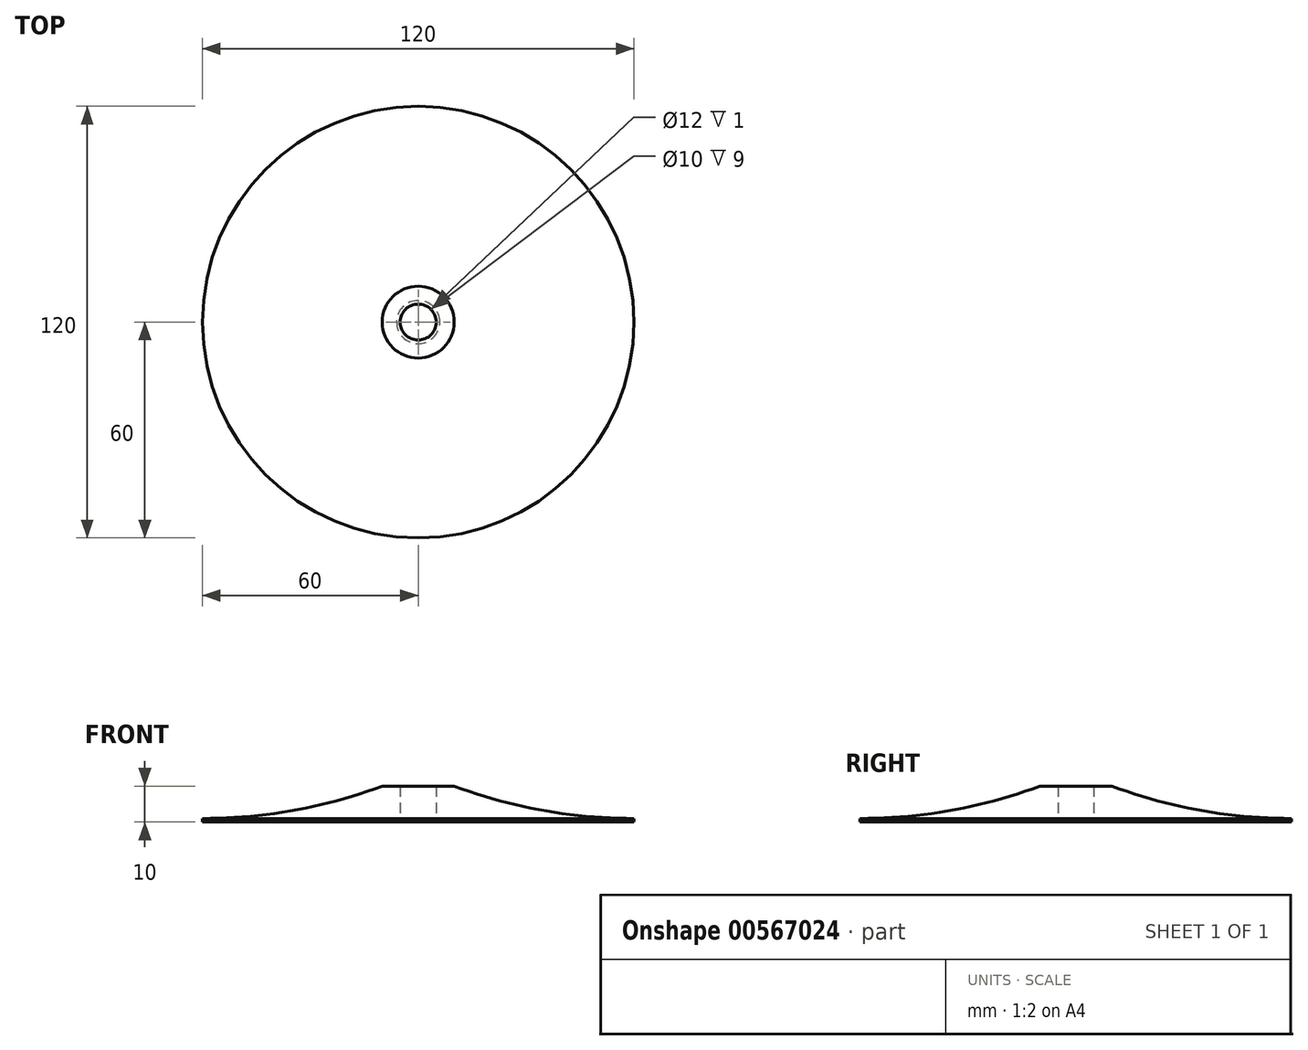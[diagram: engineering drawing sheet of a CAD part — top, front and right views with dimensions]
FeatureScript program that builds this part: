
annotation { "Feature Type Name" : "Feature", "Feature Type Description" : "" }
export const myFeature = defineFeature(function(context is Context, id is Id, definition is map)
    precondition{}
    {
        {
            var Q0;
            Q0=qCreatedBy(makeId("Right.planeOp"),FACE);
            var sketch = newSketch(context, id + "F0", { "sketchPlane" : qUnion([Q0])});
            skLineSegment(sketch, "E0", {"start": v(-6, 0) * mm, "end": v(-6, 1) * mm});
            skLineSegment(sketch, "E1", {"start": v(-6, 1) * mm, "end": v(-5, 1) * mm});
            skLineSegment(sketch, "E2", {"start": v(-5, 1) * mm, "end": v(-5, 10) * mm});
            skLineSegment(sketch, "E3", {"start": v(-5, 10) * mm, "end": v(-10, 10) * mm});
            skLineSegment(sketch, "E4", {"start": v(-6, 0) * mm, "end": v(-60, 0) * mm});
            skLineSegment(sketch, "E5", {"start": v(-60, 0) * mm, "end": v(-60, 1) * mm});
            skArc(sketch, "E6", {"start": v(-60, 1) * mm, "mid": v(-34.6, 3.27) * mm, "end": v(-10, 10) * mm});
            skLineSegment(sketch, "E7", {"start": v(-46.4, 1) * mm, "end": v(-60, 1) * mm, "construction": true});
            skLineSegment(sketch, "E8", {"start": v(0, 0) * mm, "end": v(0, 23.77) * mm, "construction": true});
            skSolve(sketch);
        }
        {
            var Q0;
            Q0=makeQuery(id+"F0.imprint","IMPRINT",FACE,{"disambiguationData":[TD([[makeQuery(id+"F0.imprint","IMPRINT",EDGE,{"derivedFrom":sQuery(id+"F0.wireOp",EDGE,"E0")}),1.0]])]});
            var Q1;
            Q1=sQuery(id+"F0.wireOp",EDGE,"E8");
            revolve(context, id + "F1", {"entities" : qUnion([Q0]), "axis" : qUnion([Q1]), "revolveType" : RevolveType.FULL});
        }
    });
